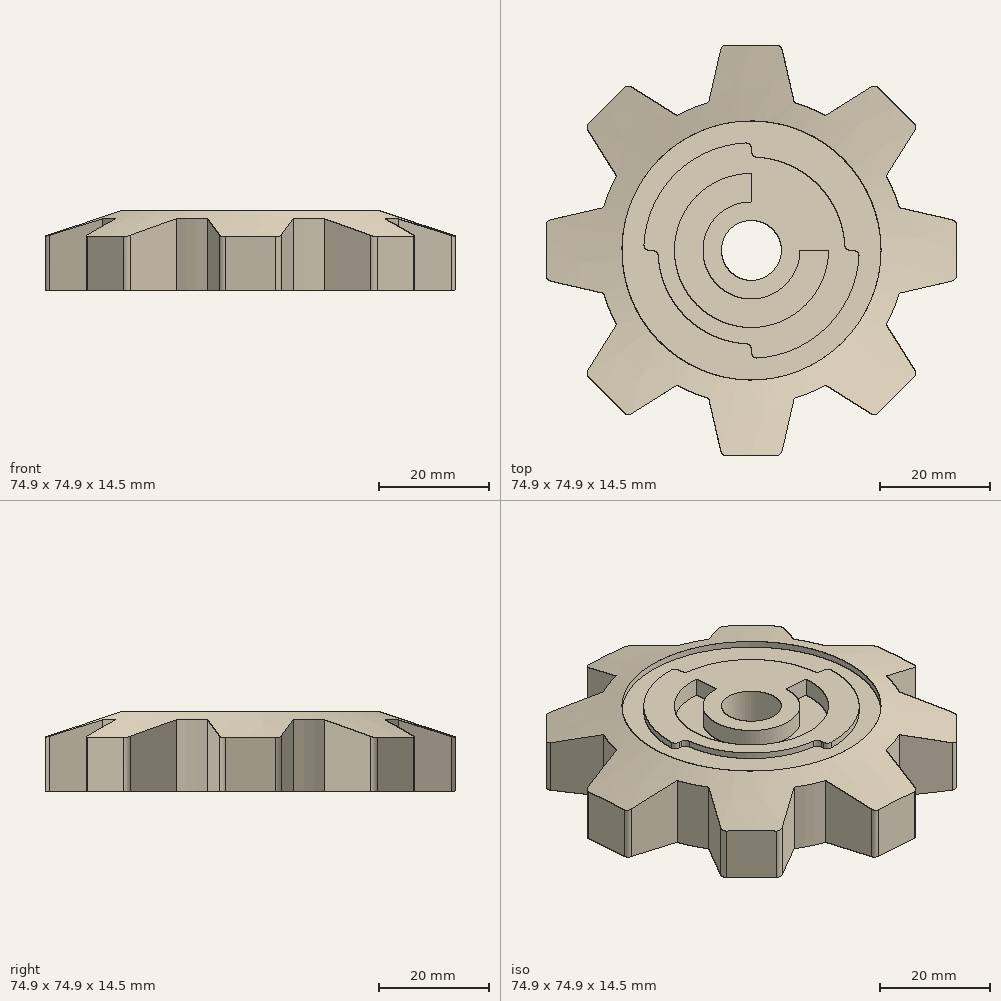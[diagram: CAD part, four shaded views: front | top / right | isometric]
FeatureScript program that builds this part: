
annotation { "Feature Type Name" : "Feature", "Feature Type Description" : "" }
export const myFeature = defineFeature(function(context is Context, id is Id, definition is map)
    precondition{}
    {
        {
            var Q0;
            Q0=qCreatedBy(makeId("Top.planeOp"),FACE);
            var sketch = newSketch(context, id + "F0", { "sketchPlane" : qUnion([Q0])});
            skArc(sketch, "E0", {"start": v(-24.63, 13.57) * mm, "mid": v(-25.98, 10.76) * mm, "end": v(-27, 7.82) * mm});
            skLineSegment(sketch, "E1", {"start": v(-5.43, 37.45) * mm, "end": v(5.43, 37.45) * mm});
            skLineSegment(sketch, "E2", {"start": v(0, 0) * mm, "end": v(0, 37.45) * mm, "construction": true});
            skLineSegment(sketch, "E3", {"start": v(-5.43, 37.45) * mm, "end": v(-7.82, 27) * mm});
            skLineSegment(sketch, "E4.MirrorCS", {"start": v(5.43, 37.45) * mm, "end": v(7.82, 27) * mm});
            skLineSegment(sketch, "E5.1.0", {"start": v(-22.64, 30.32) * mm, "end": v(-13.57, 24.63) * mm});
            skLineSegment(sketch, "E5.1.1", {"start": v(-30.32, 22.64) * mm, "end": v(-22.64, 30.32) * mm});
            skLineSegment(sketch, "E5.1.2", {"start": v(-30.32, 22.64) * mm, "end": v(-24.63, 13.57) * mm});
            skLineSegment(sketch, "E5.2.0", {"start": v(-37.45, 5.43) * mm, "end": v(-27, 7.82) * mm});
            skLineSegment(sketch, "E5.2.1", {"start": v(-37.45, -5.43) * mm, "end": v(-37.45, 5.43) * mm});
            skLineSegment(sketch, "E5.2.2", {"start": v(-37.45, -5.43) * mm, "end": v(-27, -7.82) * mm});
            skLineSegment(sketch, "E5.3.0", {"start": v(-30.32, -22.64) * mm, "end": v(-24.63, -13.57) * mm});
            skLineSegment(sketch, "E5.3.1", {"start": v(-22.64, -30.32) * mm, "end": v(-30.32, -22.64) * mm});
            skLineSegment(sketch, "E5.3.2", {"start": v(-22.64, -30.32) * mm, "end": v(-13.57, -24.63) * mm});
            skLineSegment(sketch, "E5.4.0", {"start": v(-5.43, -37.45) * mm, "end": v(-7.82, -27) * mm});
            skLineSegment(sketch, "E5.4.1", {"start": v(5.43, -37.45) * mm, "end": v(-5.43, -37.45) * mm});
            skLineSegment(sketch, "E5.4.2", {"start": v(5.43, -37.45) * mm, "end": v(7.82, -27) * mm});
            skLineSegment(sketch, "E5.5.0", {"start": v(22.64, -30.32) * mm, "end": v(13.57, -24.63) * mm});
            skLineSegment(sketch, "E5.5.1", {"start": v(30.32, -22.64) * mm, "end": v(22.64, -30.32) * mm});
            skLineSegment(sketch, "E5.5.2", {"start": v(30.32, -22.64) * mm, "end": v(24.63, -13.57) * mm});
            skLineSegment(sketch, "E5.6.0", {"start": v(37.45, -5.43) * mm, "end": v(27, -7.82) * mm});
            skLineSegment(sketch, "E5.6.1", {"start": v(37.45, 5.43) * mm, "end": v(37.45, -5.43) * mm});
            skLineSegment(sketch, "E5.6.2", {"start": v(37.45, 5.43) * mm, "end": v(27, 7.82) * mm});
            skLineSegment(sketch, "E5.7.0", {"start": v(30.32, 22.64) * mm, "end": v(24.63, 13.57) * mm});
            skLineSegment(sketch, "E5.7.1", {"start": v(22.64, 30.32) * mm, "end": v(30.32, 22.64) * mm});
            skLineSegment(sketch, "E5.7.2", {"start": v(22.64, 30.32) * mm, "end": v(13.57, 24.63) * mm});
            skArc(sketch, "E6.trimOffspring", {"start": v(-27, -7.82) * mm, "mid": v(-25.98, -10.76) * mm, "end": v(-24.63, -13.57) * mm});
            skArc(sketch, "E7.trimOffspring", {"start": v(-13.57, -24.63) * mm, "mid": v(-10.76, -25.98) * mm, "end": v(-7.82, -27) * mm});
            skArc(sketch, "E8.trimOffspring", {"start": v(7.82, -27) * mm, "mid": v(10.76, -25.98) * mm, "end": v(13.57, -24.63) * mm});
            skArc(sketch, "E9.trimOffspring", {"start": v(24.63, -13.57) * mm, "mid": v(25.98, -10.76) * mm, "end": v(27, -7.82) * mm});
            skArc(sketch, "E10.trimOffspring", {"start": v(27, 7.82) * mm, "mid": v(25.98, 10.76) * mm, "end": v(24.63, 13.57) * mm});
            skArc(sketch, "E11.trimOffspring", {"start": v(13.57, 24.63) * mm, "mid": v(10.76, 25.98) * mm, "end": v(7.82, 27) * mm});
            skArc(sketch, "E12.trimOffspring", {"start": v(-7.82, 27) * mm, "mid": v(-10.76, 25.98) * mm, "end": v(-13.57, 24.63) * mm});
            skSolve(sketch);
        }
        {
            var Q0;
            Q0=makeQuery(id+"F0.imprint","IMPRINT",FACE,{"disambiguationData":[TD([[makeQuery(id+"F0.imprint","IMPRINT",EDGE,{"derivedFrom":sQuery(id+"F0.wireOp",EDGE,"E0")}),1.0]])]});
            extrude(context, id + "F1", {"entities" : qUnion([Q0]), "depth" : 14.48 * mm, "offsetDistance" : 25.4 * mm});
        }
        {
            var Q0;
            Q0=qCreatedBy(makeId("Front.planeOp"),FACE);
            var sketch = newSketch(context, id + "F2", { "sketchPlane" : qUnion([Q0])});
            skLineSegment(sketch, "E13", {"start": v(0, 0) * mm, "end": v(0, 42.73) * mm, "construction": true});
            skSolve(sketch);
        }
        {
            var Q0;
            Q0=qCreatedBy(makeId("Front.planeOp"),FACE);
            var sketch = newSketch(context, id + "F3", { "sketchPlane" : qUnion([Q0])});
            skLineSegment(sketch, "E14.0", {"start": v(-23.68, 14.48) * mm, "end": v(23.68, 14.48) * mm, "construction": true});
            skLineSegment(sketch, "E15", {"start": v(-39.19, 9.3) * mm, "end": v(-39.19, 17.52) * mm});
            skLineSegment(sketch, "E16", {"start": v(-39.19, 17.52) * mm, "end": v(-23.68, 17.52) * mm});
            skLineSegment(sketch, "E17", {"start": v(-23.68, 17.52) * mm, "end": v(-23.68, 14.48) * mm});
            skLineSegment(sketch, "E18", {"start": v(-23.68, 14.48) * mm, "end": v(-39.19, 9.3) * mm});
            skSolve(sketch);
        }
        {
            var Q0;
            Q0=makeQuery(id+"F3.imprint","IMPRINT",FACE,{"disambiguationData":[TD([[makeQuery(id+"F3.imprint","IMPRINT",EDGE,{"derivedFrom":sQuery(id+"F3.wireOp",EDGE,"E15")}),-1.0]])]});
            var Q1;
            Q1=sQuery(id+"F2.wireOp",EDGE,"E13");
            revolve(context, id + "F4", {"operationType" : NewBodyOperationType.REMOVE, "entities" : qUnion([Q0]), "axis" : qUnion([Q1]), "revolveType" : RevolveType.FULL, "oppositeDirection" : true});
        }
        {
            var Q0;
            Q0=makeQuery(id+"F1.opExtrude","CAP_FACE",FACE,{"disambiguationData":[OSD([sQuery(id+"F0.wireOp",EDGE,"E0"),sQuery(id+"F0.wireOp",EDGE,"E1"),sQuery(id+"F0.wireOp",EDGE,"E3"),sQuery(id+"F0.wireOp",EDGE,"E4.MirrorCS"),sQuery(id+"F0.wireOp",EDGE,"E5.1.0"),sQuery(id+"F0.wireOp",EDGE,"E5.1.1"),sQuery(id+"F0.wireOp",EDGE,"E5.1.2"),sQuery(id+"F0.wireOp",EDGE,"E5.2.0"),sQuery(id+"F0.wireOp",EDGE,"E5.2.1"),sQuery(id+"F0.wireOp",EDGE,"E5.2.2"),sQuery(id+"F0.wireOp",EDGE,"E5.3.0"),sQuery(id+"F0.wireOp",EDGE,"E5.3.1"),sQuery(id+"F0.wireOp",EDGE,"E5.3.2"),sQuery(id+"F0.wireOp",EDGE,"E5.4.0"),sQuery(id+"F0.wireOp",EDGE,"E5.4.1"),sQuery(id+"F0.wireOp",EDGE,"E5.4.2"),sQuery(id+"F0.wireOp",EDGE,"E5.5.0"),sQuery(id+"F0.wireOp",EDGE,"E5.5.1"),sQuery(id+"F0.wireOp",EDGE,"E5.5.2"),sQuery(id+"F0.wireOp",EDGE,"E5.6.0"),sQuery(id+"F0.wireOp",EDGE,"E5.6.1"),sQuery(id+"F0.wireOp",EDGE,"E5.6.2"),sQuery(id+"F0.wireOp",EDGE,"E5.7.0"),sQuery(id+"F0.wireOp",EDGE,"E5.7.1"),sQuery(id+"F0.wireOp",EDGE,"E5.7.2"),sQuery(id+"F0.wireOp",EDGE,"E6.trimOffspring"),sQuery(id+"F0.wireOp",EDGE,"E7.trimOffspring"),sQuery(id+"F0.wireOp",EDGE,"E8.trimOffspring"),sQuery(id+"F0.wireOp",EDGE,"E9.trimOffspring"),sQuery(id+"F0.wireOp",EDGE,"E10.trimOffspring"),sQuery(id+"F0.wireOp",EDGE,"E11.trimOffspring"),sQuery(id+"F0.wireOp",EDGE,"E12.trimOffspring")])],"isStart":false});
            var sketch = newSketch(context, id + "F5", { "sketchPlane" : qUnion([Q0])});
            skCircle(sketch, "E19", {"center": v(0, 0) * mm, "radius": 5.46 * mm});
            skArc(sketch, "E20", {"start": v(0, 14.08) * mm, "mid": v(-9.96, -9.96) * mm, "end": v(14.08, 0) * mm});
            skArc(sketch, "E21", {"start": v(0, 19.68) * mm, "mid": v(-13.91, 13.91) * mm, "end": v(-19.68, 0) * mm});
            skArc(sketch, "E22", {"start": v(-17.07, 0) * mm, "mid": v(-12.07, -12.07) * mm, "end": v(0, -17.07) * mm});
            skCircle(sketch, "E23", {"center": v(0, 0) * mm, "radius": 23.66 * mm});
            skArc(sketch, "E24", {"start": v(0, 8.86) * mm, "mid": v(-6.26, -6.26) * mm, "end": v(8.86, 0) * mm});
            skLineSegment(sketch, "E25.trimOffspring", {"start": v(0, 8.86) * mm, "end": v(0, 14.08) * mm});
            skLineSegment(sketch, "E26.trimOffspring", {"start": v(8.86, 0) * mm, "end": v(14.08, 0) * mm});
            skLineSegment(sketch, "E27.trimOffspring", {"start": v(17.07, 0) * mm, "end": v(19.68, 0) * mm});
            skLineSegment(sketch, "E28.trimOffspring", {"start": v(0, 17.07) * mm, "end": v(0, 19.68) * mm});
            skLineSegment(sketch, "E29.trimOffspring", {"start": v(-17.07, 0) * mm, "end": v(-19.68, 0) * mm});
            skLineSegment(sketch, "E30.trimOffspring", {"start": v(0, -17.07) * mm, "end": v(0, -19.68) * mm});
            skArc(sketch, "E31.trimOffspring", {"start": v(17.07, 0) * mm, "mid": v(12.07, 12.07) * mm, "end": v(0, 17.07) * mm});
            skArc(sketch, "E32.trimOffspring", {"start": v(0, -19.68) * mm, "mid": v(13.91, -13.91) * mm, "end": v(19.68, 0) * mm});
            skSolve(sketch);
        }
        {
            var Q0;
            Q0=makeQuery(id+"F5.imprint","IMPRINT",FACE,{"disambiguationData":[TD([[makeQuery(id+"F5.imprint","IMPRINT",EDGE,{"derivedFrom":sQuery(id+"F5.wireOp",EDGE,"E21")}),-1.0]])]});
            extrude(context, id + "F6", {"entities" : qUnion([Q0]), "operationType" : NewBodyOperationType.REMOVE, "oppositeDirection" : true, "depth" : 1.2 * mm, "offsetDistance" : 25.4 * mm});
        }
        {
            var Q0;
            Q0=makeQuery(id+"F5.imprint","IMPRINT",FACE,{"disambiguationData":[TD([[makeQuery(id+"F5.imprint","IMPRINT",EDGE,{"derivedFrom":sQuery(id+"F5.wireOp",EDGE,"E19")}),1.0]])]});
            extrude(context, id + "F7", {"entities" : qUnion([Q0]), "operationType" : NewBodyOperationType.REMOVE, "oppositeDirection" : true, "depth" : 18.03 * mm, "offsetDistance" : 25.4 * mm});
        }
        {
            var Q0;
            Q0=makeQuery(id+"F5.imprint","IMPRINT",FACE,{"disambiguationData":[TD([[makeQuery(id+"F5.imprint","IMPRINT",EDGE,{"derivedFrom":sQuery(id+"F5.wireOp",EDGE,"E20")}),1.0]])]});
            extrude(context, id + "F8", {"entities" : qUnion([Q0]), "operationType" : NewBodyOperationType.REMOVE, "oppositeDirection" : true, "depth" : 3.38 * mm, "offsetDistance" : 25.4 * mm});
        }
        {
            var Q0;
            Q0=makeQuery(id+"F1.opExtrude","SWEPT_EDGE",EDGE,{"disambiguationData":[OSD([sQuery(id+"F0.wireOp",EDGE,"E5.2.1"),sQuery(id+"F0.wireOp",EDGE,"E5.2.2")])]});
            var Q1;
            Q1=makeQuery(id+"F1.opExtrude","SWEPT_EDGE",EDGE,{"disambiguationData":[OSD([sQuery(id+"F0.wireOp",EDGE,"E5.2.0"),sQuery(id+"F0.wireOp",EDGE,"E5.2.1")])]});
            var Q2;
            Q2=makeQuery(id+"F1.opExtrude","SWEPT_EDGE",EDGE,{"disambiguationData":[OSD([sQuery(id+"F0.wireOp",EDGE,"E5.3.0"),sQuery(id+"F0.wireOp",EDGE,"E5.3.1")])]});
            var Q3;
            Q3=makeQuery(id+"F1.opExtrude","SWEPT_EDGE",EDGE,{"disambiguationData":[OSD([sQuery(id+"F0.wireOp",EDGE,"E5.3.1"),sQuery(id+"F0.wireOp",EDGE,"E5.3.2")])]});
            var Q4;
            Q4=makeQuery(id+"F1.opExtrude","SWEPT_EDGE",EDGE,{"disambiguationData":[OSD([sQuery(id+"F0.wireOp",EDGE,"E5.4.0"),sQuery(id+"F0.wireOp",EDGE,"E5.4.1")])]});
            var Q5;
            Q5=makeQuery(id+"F1.opExtrude","SWEPT_EDGE",EDGE,{"disambiguationData":[OSD([sQuery(id+"F0.wireOp",EDGE,"E5.4.1"),sQuery(id+"F0.wireOp",EDGE,"E5.4.2")])]});
            var Q6;
            Q6=makeQuery(id+"F1.opExtrude","SWEPT_EDGE",EDGE,{"disambiguationData":[OSD([sQuery(id+"F0.wireOp",EDGE,"E5.5.0"),sQuery(id+"F0.wireOp",EDGE,"E5.5.1")])]});
            var Q7;
            Q7=makeQuery(id+"F1.opExtrude","SWEPT_EDGE",EDGE,{"disambiguationData":[OSD([sQuery(id+"F0.wireOp",EDGE,"E5.5.1"),sQuery(id+"F0.wireOp",EDGE,"E5.5.2")])]});
            var Q8;
            Q8=makeQuery(id+"F1.opExtrude","SWEPT_EDGE",EDGE,{"disambiguationData":[OSD([sQuery(id+"F0.wireOp",EDGE,"E5.6.0"),sQuery(id+"F0.wireOp",EDGE,"E5.6.1")])]});
            var Q9;
            Q9=makeQuery(id+"F1.opExtrude","SWEPT_EDGE",EDGE,{"disambiguationData":[OSD([sQuery(id+"F0.wireOp",EDGE,"E5.6.1"),sQuery(id+"F0.wireOp",EDGE,"E5.6.2")])]});
            var Q10;
            Q10=makeQuery(id+"F1.opExtrude","SWEPT_EDGE",EDGE,{"disambiguationData":[OSD([sQuery(id+"F0.wireOp",EDGE,"E5.7.0"),sQuery(id+"F0.wireOp",EDGE,"E5.7.1")])]});
            var Q11;
            Q11=makeQuery(id+"F1.opExtrude","SWEPT_EDGE",EDGE,{"disambiguationData":[OSD([sQuery(id+"F0.wireOp",EDGE,"E5.7.1"),sQuery(id+"F0.wireOp",EDGE,"E5.7.2")])]});
            var Q12;
            Q12=makeQuery(id+"F1.opExtrude","SWEPT_EDGE",EDGE,{"disambiguationData":[OSD([sQuery(id+"F0.wireOp",EDGE,"E1"),sQuery(id+"F0.wireOp",EDGE,"E4.MirrorCS")])]});
            var Q13;
            Q13=makeQuery(id+"F1.opExtrude","SWEPT_EDGE",EDGE,{"disambiguationData":[OSD([sQuery(id+"F0.wireOp",EDGE,"E1"),sQuery(id+"F0.wireOp",EDGE,"E3")])]});
            var Q14;
            Q14=makeQuery(id+"F1.opExtrude","SWEPT_EDGE",EDGE,{"disambiguationData":[OSD([sQuery(id+"F0.wireOp",EDGE,"E5.1.1"),sQuery(id+"F0.wireOp",EDGE,"E5.1.2")])]});
            var Q15;
            Q15=makeQuery(id+"F1.opExtrude","SWEPT_EDGE",EDGE,{"disambiguationData":[OSD([sQuery(id+"F0.wireOp",EDGE,"E5.1.0"),sQuery(id+"F0.wireOp",EDGE,"E5.1.1")])]});
            var Q16;
            Q16=makeQuery(id+"F6.boolean.opBoolean","COPY",EDGE,{"derivedFrom":makeQuery(id+"F6.opExtrude","SWEPT_EDGE",EDGE,{"disambiguationData":[OSD([sQuery(id+"F5.wireOp",EDGE,"E27.trimOffspring"),sQuery(id+"F5.wireOp",EDGE,"E32.trimOffspring")])]})});
            var Q17;
            Q17=makeQuery(id+"F6.boolean.opBoolean","COPY",EDGE,{"derivedFrom":makeQuery(id+"F6.opExtrude","SWEPT_EDGE",EDGE,{"disambiguationData":[OSD([sQuery(id+"F5.wireOp",EDGE,"E27.trimOffspring"),sQuery(id+"F5.wireOp",EDGE,"E31.trimOffspring")])]})});
            var Q18;
            Q18=makeQuery(id+"F6.boolean.opBoolean","COPY",EDGE,{"derivedFrom":makeQuery(id+"F6.opExtrude","SWEPT_EDGE",EDGE,{"disambiguationData":[OSD([sQuery(id+"F5.wireOp",EDGE,"E28.trimOffspring"),sQuery(id+"F5.wireOp",EDGE,"E31.trimOffspring")])]})});
            var Q19;
            Q19=makeQuery(id+"F6.boolean.opBoolean","COPY",EDGE,{"derivedFrom":makeQuery(id+"F6.opExtrude","SWEPT_EDGE",EDGE,{"disambiguationData":[OSD([sQuery(id+"F5.wireOp",EDGE,"E21"),sQuery(id+"F5.wireOp",EDGE,"E28.trimOffspring")])]})});
            var Q20;
            Q20=makeQuery(id+"F8.opExtrude","SWEPT_EDGE",EDGE,{"disambiguationData":[OSD([sQuery(id+"F5.wireOp",EDGE,"E20"),sQuery(id+"F5.wireOp",EDGE,"E25.trimOffspring")])]});
            var Q21;
            Q21=makeQuery(id+"F8.opExtrude","SWEPT_EDGE",EDGE,{"disambiguationData":[OSD([sQuery(id+"F5.wireOp",EDGE,"E24"),sQuery(id+"F5.wireOp",EDGE,"E25.trimOffspring")])]});
            var Q22;
            Q22=makeQuery(id+"F8.opExtrude","SWEPT_EDGE",EDGE,{"disambiguationData":[OSD([sQuery(id+"F5.wireOp",EDGE,"E24"),sQuery(id+"F5.wireOp",EDGE,"E26.trimOffspring")])]});
            var Q23;
            Q23=makeQuery(id+"F8.opExtrude","SWEPT_EDGE",EDGE,{"disambiguationData":[OSD([sQuery(id+"F5.wireOp",EDGE,"E20"),sQuery(id+"F5.wireOp",EDGE,"E26.trimOffspring")])]});
            var Q24;
            Q24=makeQuery(id+"F7.boolean.opBoolean","COPY",EDGE,{"derivedFrom":makeQuery(id+"F7.opExtrude","CAP_EDGE",EDGE,{"disambiguationData":[OSD([sQuery(id+"F5.wireOp",EDGE,"E19")])],"isStart":true})});
            var Q25;
            Q25=makeQuery(id+"F6.boolean.opBoolean","COPY",EDGE,{"derivedFrom":makeQuery(id+"F6.opExtrude","SWEPT_EDGE",EDGE,{"disambiguationData":[OSD([sQuery(id+"F5.wireOp",EDGE,"E21"),sQuery(id+"F5.wireOp",EDGE,"E29.trimOffspring")])]})});
            var Q26;
            Q26=makeQuery(id+"F6.boolean.opBoolean","COPY",EDGE,{"derivedFrom":makeQuery(id+"F6.opExtrude","SWEPT_EDGE",EDGE,{"disambiguationData":[OSD([sQuery(id+"F5.wireOp",EDGE,"E22"),sQuery(id+"F5.wireOp",EDGE,"E29.trimOffspring")])]})});
            var Q27;
            Q27=makeQuery(id+"F6.boolean.opBoolean","COPY",EDGE,{"derivedFrom":makeQuery(id+"F6.opExtrude","SWEPT_EDGE",EDGE,{"disambiguationData":[OSD([sQuery(id+"F5.wireOp",EDGE,"E30.trimOffspring"),sQuery(id+"F5.wireOp",EDGE,"E32.trimOffspring")])]})});
            var Q28;
            Q28=makeQuery(id+"F6.boolean.opBoolean","COPY",EDGE,{"derivedFrom":makeQuery(id+"F6.opExtrude","SWEPT_EDGE",EDGE,{"disambiguationData":[OSD([sQuery(id+"F5.wireOp",EDGE,"E22"),sQuery(id+"F5.wireOp",EDGE,"E30.trimOffspring")])]})});
            fillet(context, id + "F9", {"entities" : qUnion([Q0, Q1, Q2, Q3, Q4, Q5, Q6, Q7, Q8, Q9, Q10, Q11, Q12, Q13, Q14, Q15, Q16, Q17, Q18, Q19, Q20, Q21, Q22, Q23, Q24, Q25, Q26, Q27, Q28]), "radius" : 1.02 * mm, "tangentPropagation" : true, "allowEdgeOverflow" : false});
        }
    });
